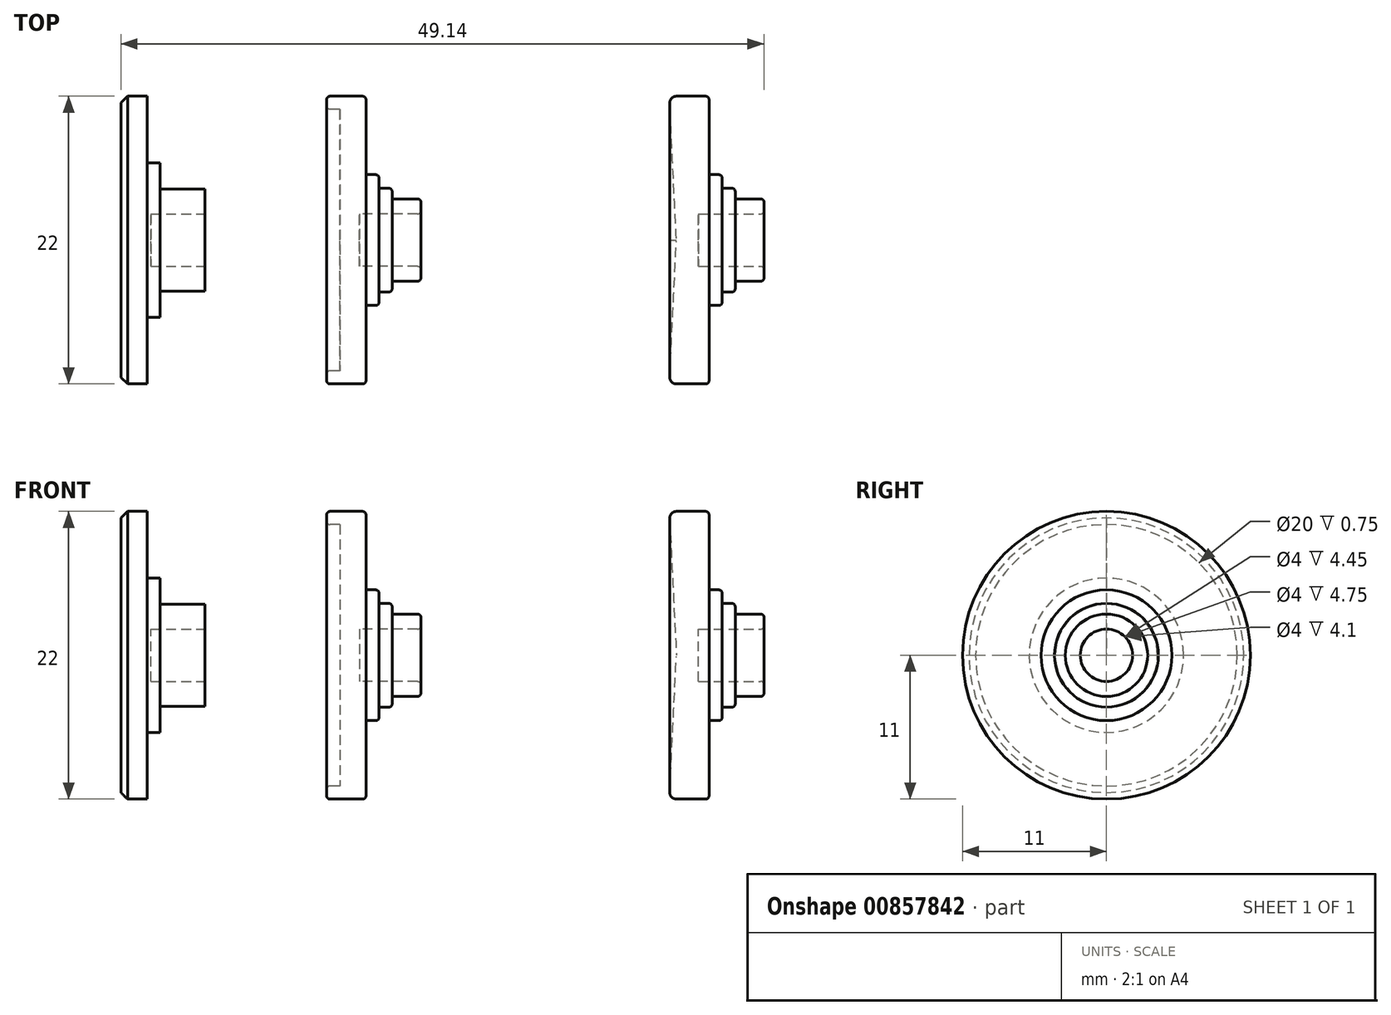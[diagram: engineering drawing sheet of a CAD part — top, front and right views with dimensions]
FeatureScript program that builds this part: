
annotation { "Feature Type Name" : "Feature", "Feature Type Description" : "" }
export const myFeature = defineFeature(function(context is Context, id is Id, definition is map)
    precondition{}
    {
        {
            var Q0;
            Q0=qCreatedBy(makeId("Front.planeOp"),FACE);
            var sketch = newSketch(context, id + "F0", { "sketchPlane" : qUnion([Q0])});
            skLineSegment(sketch, "E0", {"start": v(0, 0) * mm, "end": v(0, 10.5) * mm});
            skLineSegment(sketch, "E1", {"start": v(0.5, 11) * mm, "end": v(2, 11) * mm});
            skLineSegment(sketch, "E2", {"start": v(2, 11) * mm, "end": v(2, 5.9) * mm});
            skLineSegment(sketch, "E3", {"start": v(2, 5.9) * mm, "end": v(3, 5.9) * mm});
            skLineSegment(sketch, "E4", {"start": v(3, 5.9) * mm, "end": v(3, 3.9) * mm});
            skLineSegment(sketch, "E5", {"start": v(3, 3.9) * mm, "end": v(6.4, 3.9) * mm});
            skLineSegment(sketch, "E6", {"start": v(6.4, 3.9) * mm, "end": v(6.4, 2) * mm});
            skLineSegment(sketch, "E7", {"start": v(6.4, 2) * mm, "end": v(2.3, 2) * mm});
            skLineSegment(sketch, "E8", {"start": v(2.3, 2) * mm, "end": v(2.3, 0) * mm});
            skLineSegment(sketch, "E9", {"start": v(2.3, 0) * mm, "end": v(0, 0) * mm});
            skLineSegment(sketch, "E10", {"start": v(2, 11) * mm, "end": v(0.5, 11) * mm});
            skLineSegment(sketch, "E11", {"start": v(0, 10.5) * mm, "end": v(0.5, 11) * mm});
            skSolve(sketch);
        }
        {
            var Q0;
            Q0=makeQuery(id+"F0.imprint","IMPRINT",FACE,{"disambiguationData":[TD([[makeQuery(id+"F0.imprint","IMPRINT",EDGE,{"derivedFrom":sQuery(id+"F0.wireOp",EDGE,"E2")}),-1.0]])]});
            var Q1;
            Q1=sQuery(id+"F0.wireOp",EDGE,"E9");
            revolve(context, id + "F1", {"surfaceOperationType" : NewSurfaceOperationType.NEW, "entities" : qUnion([Q0]), "axis" : qUnion([Q1]), "revolveType" : RevolveType.FULL});
        }
        {
            var Q0;
            Q0=qCreatedBy(makeId("Front.planeOp"),FACE);
            var sketch = newSketch(context, id + "F2", { "sketchPlane" : qUnion([Q0])});
            skLineSegment(sketch, "E12", {"start": v(18.72, 10.75) * mm, "end": v(18.72, 5) * mm});
            skLineSegment(sketch, "E13", {"start": v(18.72, 5) * mm, "end": v(19.47, 5) * mm});
            skLineSegment(sketch, "E14", {"start": v(19.72, 4.75) * mm, "end": v(19.72, 3.97) * mm});
            skLineSegment(sketch, "E15", {"start": v(22.67, 2) * mm, "end": v(18.22, 2) * mm});
            skLineSegment(sketch, "E16", {"start": v(18.22, 2) * mm, "end": v(18.22, 0) * mm});
            skLineSegment(sketch, "E17", {"start": v(18.47, 11) * mm, "end": v(15.97, 11) * mm});
            skLineSegment(sketch, "E18", {"start": v(19.72, 3.97) * mm, "end": v(20.47, 3.97) * mm});
            skLineSegment(sketch, "E19", {"start": v(22.92, 2.25) * mm, "end": v(22.92, 2.9) * mm});
            skLineSegment(sketch, "E20", {"start": v(22.67, 3.15) * mm, "end": v(20.72, 3.15) * mm});
            skLineSegment(sketch, "E21", {"start": v(20.72, 3.15) * mm, "end": v(20.72, 3.72) * mm});
            skLineSegment(sketch, "E22", {"start": v(15.72, 10.75) * mm, "end": v(15.72, 10.25) * mm});
            skLineSegment(sketch, "E23", {"start": v(15.97, 10) * mm, "end": v(16.72, 10) * mm});
            skLineSegment(sketch, "E24", {"start": v(16.72, 10) * mm, "end": v(16.72, 0) * mm});
            skPoint(sketch, "E25.visualSharp", {"position": v(15.72, 11) * mm});
            skArc(sketch, "E25.filletArc", {"start": v(15.97, 11) * mm, "mid": v(15.8, 10.93) * mm, "end": v(15.72, 10.75) * mm});
            skPoint(sketch, "E26.visualSharp", {"position": v(15.72, 10) * mm});
            skArc(sketch, "E26.filletArc", {"start": v(15.72, 10.25) * mm, "mid": v(15.8, 10.07) * mm, "end": v(15.97, 10) * mm});
            skPoint(sketch, "E27.visualSharp", {"position": v(18.72, 11) * mm});
            skArc(sketch, "E27.filletArc", {"start": v(18.72, 10.75) * mm, "mid": v(18.65, 10.93) * mm, "end": v(18.47, 11) * mm});
            skPoint(sketch, "E28.visualSharp", {"position": v(20.72, 3.97) * mm});
            skArc(sketch, "E28.filletArc", {"start": v(20.72, 3.72) * mm, "mid": v(20.65, 3.9) * mm, "end": v(20.47, 3.97) * mm});
            skPoint(sketch, "E29.visualSharp", {"position": v(22.92, 3.15) * mm});
            skArc(sketch, "E29.filletArc", {"start": v(22.92, 2.9) * mm, "mid": v(22.85, 3.08) * mm, "end": v(22.67, 3.15) * mm});
            skPoint(sketch, "E30.visualSharp", {"position": v(19.72, 5) * mm});
            skArc(sketch, "E30.filletArc", {"start": v(19.72, 4.75) * mm, "mid": v(19.65, 4.93) * mm, "end": v(19.47, 5) * mm});
            skPoint(sketch, "E31.visualSharp", {"position": v(22.92, 2) * mm});
            skArc(sketch, "E31.filletArc", {"start": v(22.67, 2) * mm, "mid": v(22.85, 2.07) * mm, "end": v(22.92, 2.25) * mm});
            skLineSegment(sketch, "E32", {"start": v(16.72, 0) * mm, "end": v(18.22, 0) * mm});
            skSolve(sketch);
        }
        {
            var Q0;
            Q0=qCreatedBy(makeId("Front.planeOp"),FACE);
            var sketch = newSketch(context, id + "F3", { "sketchPlane" : qUnion([Q0])});
            skLineSegment(sketch, "E33", {"start": v(44.94, 10.75) * mm, "end": v(44.94, 5) * mm});
            skLineSegment(sketch, "E34", {"start": v(44.94, 5) * mm, "end": v(45.7, 5) * mm});
            skLineSegment(sketch, "E35", {"start": v(45.94, 4.75) * mm, "end": v(45.94, 3.97) * mm});
            skLineSegment(sketch, "E36", {"start": v(48.9, 2) * mm, "end": v(44.14, 2) * mm});
            skLineSegment(sketch, "E37", {"start": v(44.14, 2) * mm, "end": v(44.14, 0) * mm});
            skLineSegment(sketch, "E38", {"start": v(44.7, 11) * mm, "end": v(42.44, 11) * mm});
            skLineSegment(sketch, "E39", {"start": v(45.94, 3.97) * mm, "end": v(46.7, 3.97) * mm});
            skLineSegment(sketch, "E40", {"start": v(49.14, 2.25) * mm, "end": v(49.14, 2.9) * mm});
            skLineSegment(sketch, "E41", {"start": v(48.9, 3.15) * mm, "end": v(46.94, 3.15) * mm});
            skLineSegment(sketch, "E42", {"start": v(46.94, 3.15) * mm, "end": v(46.94, 3.72) * mm});
            skPoint(sketch, "E43.visualSharp", {"position": v(41.94, 11) * mm});
            skPoint(sketch, "E44.visualSharp", {"position": v(44.94, 11) * mm});
            skArc(sketch, "E44.filletArc", {"start": v(44.94, 10.75) * mm, "mid": v(44.87, 10.93) * mm, "end": v(44.7, 11) * mm});
            skPoint(sketch, "E45.visualSharp", {"position": v(46.94, 3.97) * mm});
            skArc(sketch, "E45.filletArc", {"start": v(46.94, 3.72) * mm, "mid": v(46.87, 3.9) * mm, "end": v(46.7, 3.97) * mm});
            skPoint(sketch, "E46.visualSharp", {"position": v(49.14, 3.15) * mm});
            skArc(sketch, "E46.filletArc", {"start": v(49.14, 2.9) * mm, "mid": v(49.07, 3.08) * mm, "end": v(48.9, 3.15) * mm});
            skPoint(sketch, "E47.visualSharp", {"position": v(45.94, 5) * mm});
            skArc(sketch, "E47.filletArc", {"start": v(45.94, 4.75) * mm, "mid": v(45.87, 4.93) * mm, "end": v(45.7, 5) * mm});
            skPoint(sketch, "E48.visualSharp", {"position": v(49.14, 2) * mm});
            skArc(sketch, "E48.filletArc", {"start": v(48.9, 2) * mm, "mid": v(49.07, 2.07) * mm, "end": v(49.14, 2.25) * mm});
            skLineSegment(sketch, "E49", {"start": v(44.94, 11) * mm, "end": v(42.44, 11) * mm});
            skLineSegment(sketch, "E50", {"start": v(41.94, 10.5) * mm, "end": v(41.94, 10.5) * mm});
            skLineSegment(sketch, "E51", {"start": v(41.94, 0) * mm, "end": v(42.44, 0) * mm});
            skFitSpline(sketch, "E52", {"points": [v(41.94, 10.5) * mm, v(42.44, 0) * mm], "startDerivative": vector(0, -2.31) * mm, "endDerivative": vector(0, -1.55) * mm});
            skArc(sketch, "E53.filletArc", {"start": v(42.44, 11) * mm, "mid": v(42.1, 10.85) * mm, "end": v(41.94, 10.5) * mm});
            skLineSegment(sketch, "E54", {"start": v(44.14, 0) * mm, "end": v(42.44, 0) * mm});
            skSolve(sketch);
        }
        {
            var Q0;
            Q0 = qSketchRegion(id + "F2", true);
            var Q1;
            Q1=sQuery(id+"F2.wireOp",EDGE,"E32");
            revolve(context, id + "F4", {"surfaceOperationType" : NewSurfaceOperationType.NEW, "entities" : qUnion([Q0]), "axis" : qUnion([Q1]), "revolveType" : RevolveType.FULL});
        }
        {
            var Q0;
            Q0 = qSketchRegion(id + "F3", true);
            var Q1;
            Q1=sQuery(id+"F3.wireOp",EDGE,"E54");
            revolve(context, id + "F5", {"surfaceOperationType" : NewSurfaceOperationType.NEW, "entities" : qUnion([Q0]), "axis" : qUnion([Q1]), "revolveType" : RevolveType.FULL});
        }
    });
